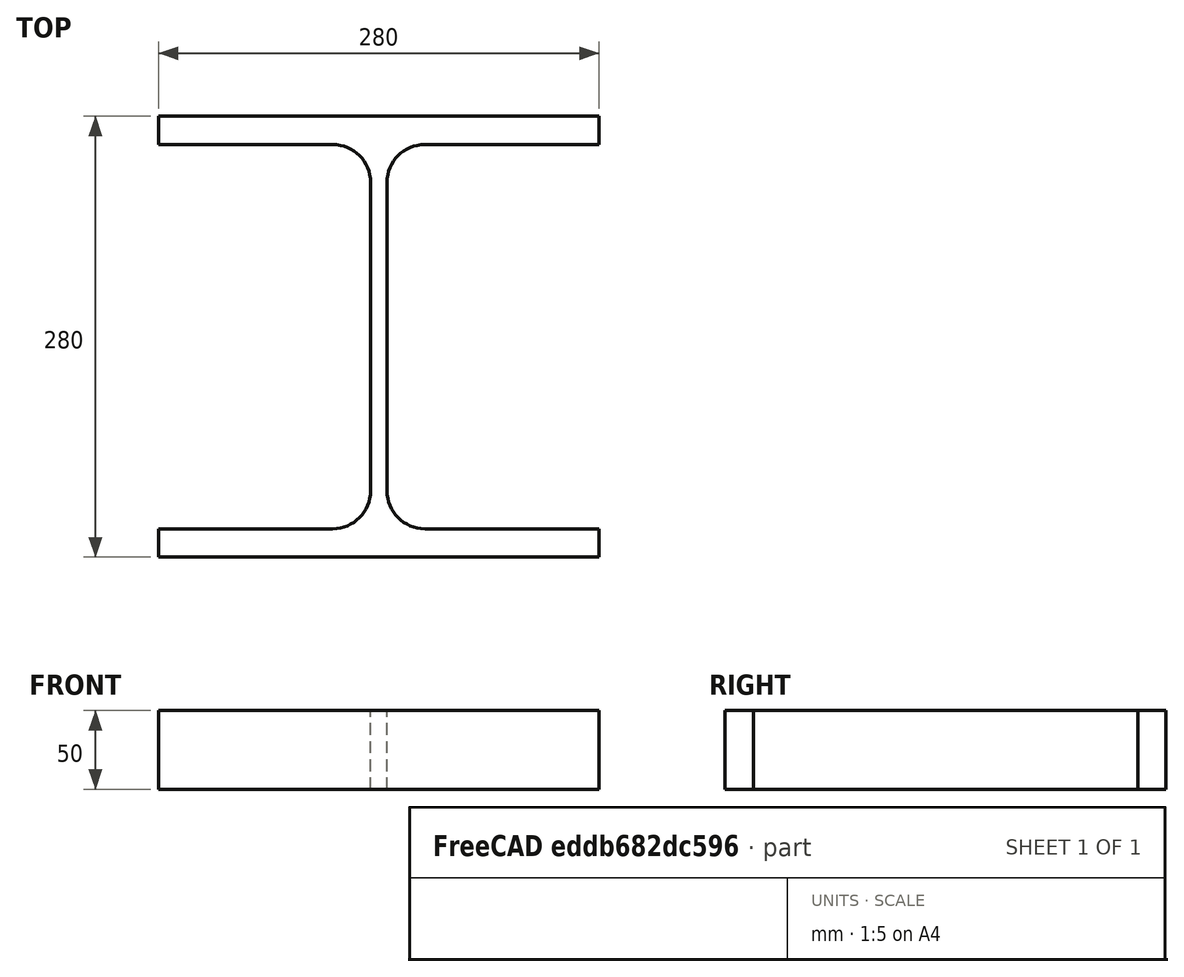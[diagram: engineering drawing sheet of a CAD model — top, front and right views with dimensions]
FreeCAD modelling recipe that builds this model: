
FCSTD DOCUMENT  (FreeCAD 0.15R4671 (Git))
Label: HE-B-Profile 280 DIN1025-2 S235JR
License: All rights reserved
LicenseURL: http://en.wikipedia.org/wiki/All_rights_reserved
objects: Sketcher::SketchObject×1, Part::Extrusion×1
note: 2 computed .brp shape members not serialized (recipe doc carries the construction recipe); baked Part::Feature solids carry a one-line shape summary decoded from their .brp

FEATURE [Sketcher::SketchObject] Sketch
  sketch-geometry (16):
    g0: LineSegment StartX=5.25 StartY=-98 StartZ=0 EndX=5.25 EndY=98 EndZ=0
    g1: LineSegment StartX=29.25 StartY=122 StartZ=0 EndX=140 EndY=122 EndZ=0
    g2: LineSegment StartX=140 StartY=122 StartZ=0 EndX=140 EndY=140 EndZ=0
    g3: LineSegment StartX=140 StartY=140 StartZ=0 EndX=-140 EndY=140 EndZ=0
    g4: LineSegment StartX=-140 StartY=140 StartZ=0 EndX=-140 EndY=122 EndZ=0
    g5: LineSegment StartX=-140 StartY=122 StartZ=0 EndX=-29.25 EndY=122 EndZ=0
    g6: LineSegment StartX=-5.25 StartY=98 StartZ=0 EndX=-5.25 EndY=-98 EndZ=0
    g7: LineSegment StartX=-29.25 StartY=-122 StartZ=0 EndX=-140 EndY=-122 EndZ=0
    g8: LineSegment StartX=-140 StartY=-122 StartZ=0 EndX=-140 EndY=-140 EndZ=0
    g9: LineSegment StartX=-140 StartY=-140 StartZ=0 EndX=140 EndY=-140 EndZ=0
    g10: LineSegment StartX=140 StartY=-140 StartZ=0 EndX=140 EndY=-122 EndZ=0
    g11: LineSegment StartX=140 StartY=-122 StartZ=0 EndX=29.25 EndY=-122 EndZ=0
    g12: ArcOfCircle CenterX=29.25 CenterY=98 CenterZ=0 NormalX=0 NormalY=0 NormalZ=1 Radius=24 StartAngle=1.5708 EndAngle=3.14159
    g13: ArcOfCircle CenterX=29.25 CenterY=-98 CenterZ=0 NormalX=0 NormalY=0 NormalZ=1 Radius=24 StartAngle=3.14159 EndAngle=4.71239
    g14: ArcOfCircle CenterX=-29.25 CenterY=98 CenterZ=0 NormalX=0 NormalY=0 NormalZ=1 Radius=24 StartAngle=0 EndAngle=1.5708
    g15: ArcOfCircle CenterX=-29.25 CenterY=-98 CenterZ=0 NormalX=0 NormalY=0 NormalZ=1 Radius=24 StartAngle=4.71239 EndAngle=6.28319
  constraints (42):
    c: Vertical(g0)
    c: Coincident(g2,g1)
    c: Vertical(g2)
    c: Coincident(g3,g2)
    c: Coincident(g4,g3)
    c: Vertical(g4)
    c: Coincident(g5,g4)
    c: Horizontal(g5)
    c: Vertical(g6)
    c: Horizontal(g7)
    c: Coincident(g8,g7)
    c: Vertical(g8)
    c: Coincident(g9,g8)
    c: Horizontal(g9)
    c: Coincident(g10,g9)
    c: Vertical(g10)
    c: Coincident(g11,g10)
    c: Horizontal(g11)
    c: Tangent(g1,g12) = 1.5708
    c: Tangent(g0,g12) = 1.5708
    c: Tangent(g0,g13) = 1.5708
    c: Tangent(g11,g13) = 1.5708
    c: Tangent(g5,g14) = 1.5708
    c: Tangent(g6,g14) = 1.5708
    c: Tangent(g6,g15) = 1.5708
    c: Tangent(g7,g15) = 1.5708
    c: Equal(g3,g9)
    c: Equal(g2,g4)
    c: Equal(g4,g8)
    c: Equal(g8,g10)
    c: Equal(g12,g14)
    c: Equal(g14,g15)
    c: Equal(g15,g13)
    c: Symmetric(g2,g3,g-2)
    c: Symmetric(g9,g8,g-2)
    c: Symmetric(g0,g6,g-2)
    c: Symmetric(g2,g9,g-1)
    c: DistanceY(g2,g9) = -280
    c: DistanceX(g3) = -280
    c: DistanceX(g0,g6) = -10.5
    c: DistanceY(g2) = 18
    c: Radius(g12) = 24
FEATURE [Part::Extrusion] Extrude  label="HE-B-Profile 280 DIN1025-2 S235JR"
  Base = -> Sketch
  Dir = (0,0,50)
  Solid = true
